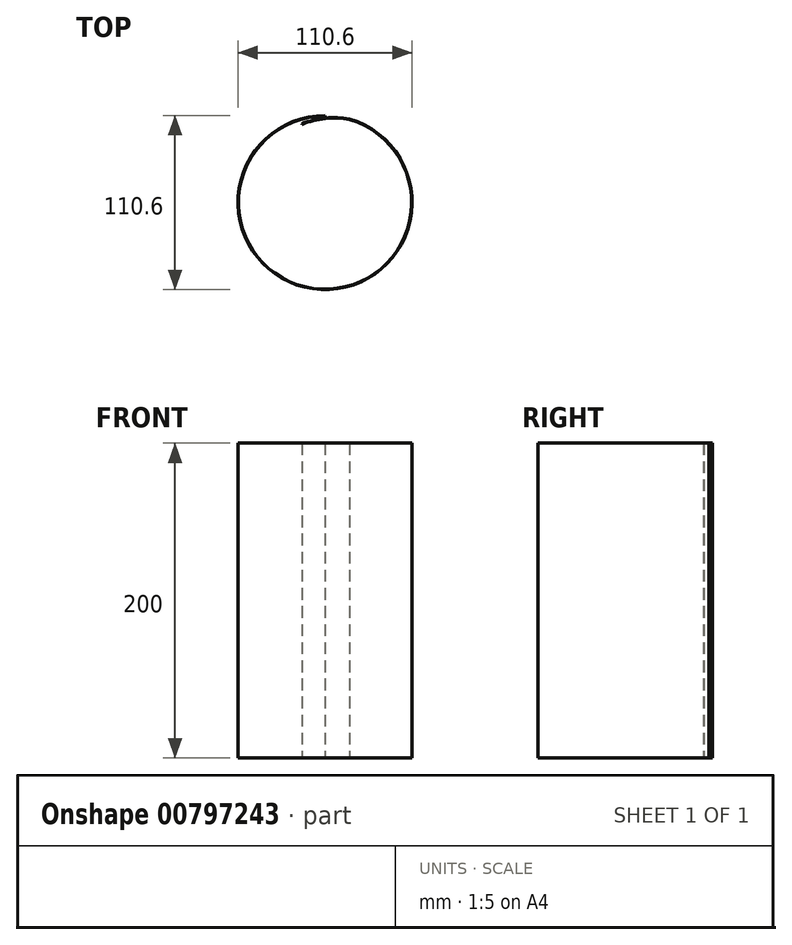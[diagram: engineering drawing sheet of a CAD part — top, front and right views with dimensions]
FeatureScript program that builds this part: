
annotation { "Feature Type Name" : "Feature", "Feature Type Description" : "" }
export const myFeature = defineFeature(function(context is Context, id is Id, definition is map)
    precondition{}
    {
        {
            var Q0;
            Q0=qCreatedBy(makeId("Top.planeOp"),FACE);
            var sketch = newSketch(context, id + "F0", { "sketchPlane" : qUnion([Q0])});
            skArc(sketch, "E0", {"start": v(0, 55.3) * mm, "mid": v(-7.8, -54.75) * mm, "end": v(15.46, 53.1) * mm});
            skLineSegment(sketch, "E1", {"start": v(-14.72, 49.97) * mm, "end": v(-14.6, 49.7) * mm});
            skArc(sketch, "E2", {"start": v(15.4, 52.8) * mm, "mid": v(-7.77, -54.45) * mm, "end": v(0, 55) * mm});
            skLineSegment(sketch, "E3", {"start": v(0, 55) * mm, "end": v(0, 55.3) * mm});
            skArc(sketch, "E4", {"start": v(15.46, 53.1) * mm, "mid": v(0.15, 53.66) * mm, "end": v(-14.72, 49.97) * mm});
            skArc(sketch, "E5", {"start": v(15.4, 52.8) * mm, "mid": v(0.17, 53.36) * mm, "end": v(-14.6, 49.7) * mm});
            skSolve(sketch);
        }
        {
            var Q0;
            Q0 = qSketchRegion(id + "F0", true);
            extrude(context, id + "F1", {"entities" : qUnion([Q0]), "depth" : 200 * mm, "offsetDistance" : 25 * mm});
        }
    });
